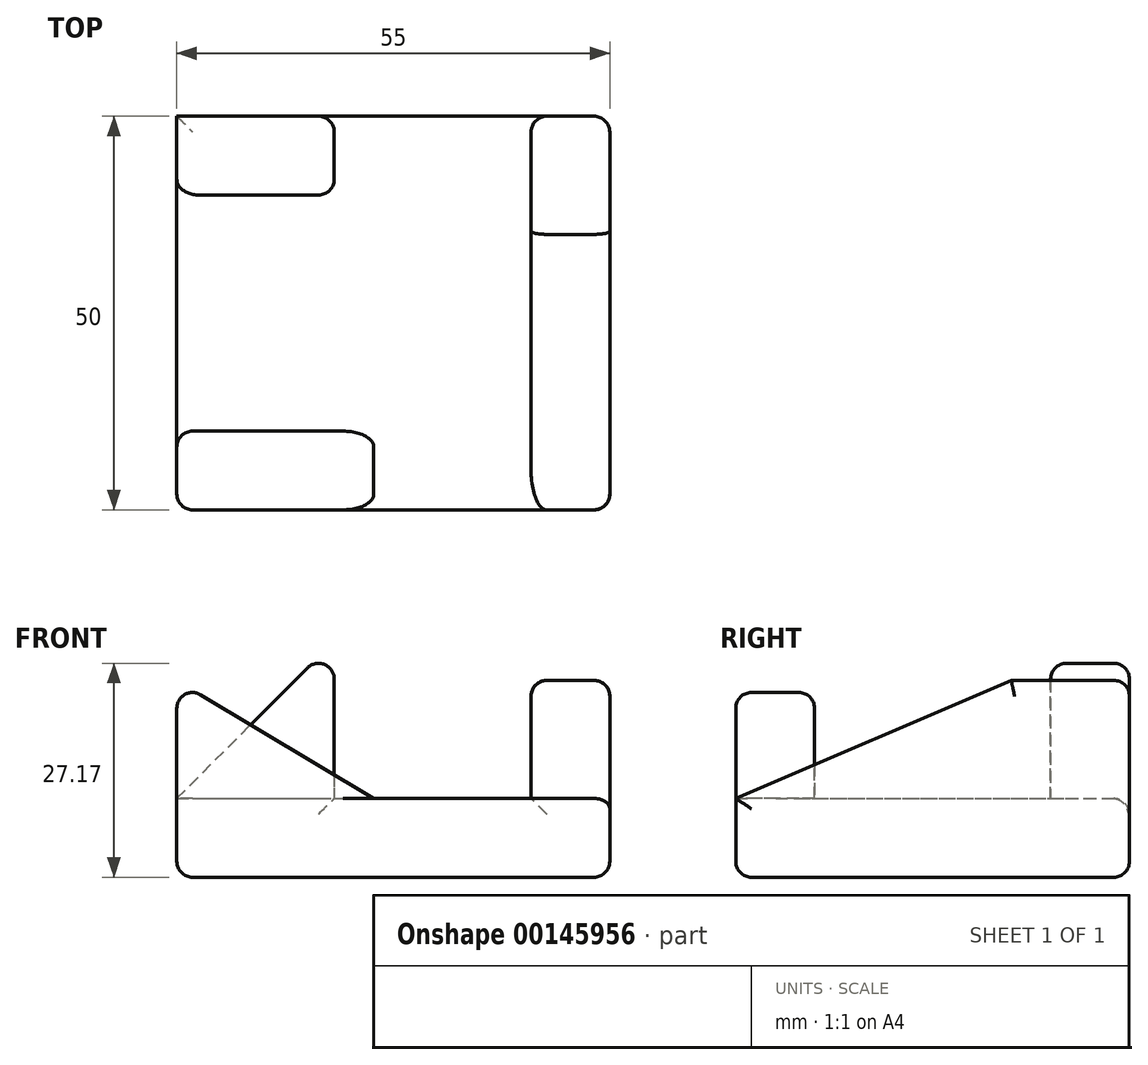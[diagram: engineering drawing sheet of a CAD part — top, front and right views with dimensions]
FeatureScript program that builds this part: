
annotation { "Feature Type Name" : "Feature", "Feature Type Description" : "" }
export const myFeature = defineFeature(function(context is Context, id is Id, definition is map)
    precondition{}
    {
        {
            var Q0;
            Q0=qCreatedBy(makeId("Top.planeOp"),FACE);
            var sketch = newSketch(context, id + "F0", { "sketchPlane" : qUnion([Q0])});
            skLineSegment(sketch, "E0.bottom", {"start": v(-27.5, -25) * mm, "end": v(27.5, -25) * mm});
            skLineSegment(sketch, "E0.top", {"start": v(-27.5, 25) * mm, "end": v(27.5, 25) * mm});
            skLineSegment(sketch, "E0.left", {"start": v(-27.5, -25) * mm, "end": v(-27.5, 25) * mm});
            skLineSegment(sketch, "E0.right", {"start": v(27.5, -25) * mm, "end": v(27.5, 25) * mm});
            skPoint(sketch, "E0.middle", {"position": v(0, 0) * mm});
            skSolve(sketch);
        }
        {
            var Q0;
            Q0 = qSketchRegion(id + "F0", true);
            extrude(context, id + "F1", {"entities" : qUnion([Q0]), "depth" : 10 * mm});
        }
        {
            var Q0;
            Q0=makeQuery(id+"F1.opExtrude","SWEPT_FACE",FACE,{"disambiguationData":[OSD([sQuery(id+"F0.wireOp",EDGE,"E0.bottom")])]});
            var sketch = newSketch(context, id + "F2", { "sketchPlane" : qUnion([Q0])});
            skLineSegment(sketch, "E1", {"start": v(-27.5, 10) * mm, "end": v(-27.5, 25) * mm});
            skLineSegment(sketch, "E2", {"start": v(-27.5, 25) * mm, "end": v(-2.5, 10) * mm});
            skLineSegment(sketch, "E3", {"start": v(-2.5, 10) * mm, "end": v(-27.5, 10) * mm});
            skSolve(sketch);
        }
        {
            var Q0;
            Q0=makeQuery(id+"F1.opExtrude","SWEPT_FACE",FACE,{"disambiguationData":[OSD([sQuery(id+"F0.wireOp",EDGE,"E0.top")])]});
            var sketch = newSketch(context, id + "F3", { "sketchPlane" : qUnion([Q0])});
            skLineSegment(sketch, "E4", {"start": v(27.5, 10) * mm, "end": v(7.5, 30) * mm});
            skLineSegment(sketch, "E5", {"start": v(7.5, 30) * mm, "end": v(7.5, 10) * mm});
            skLineSegment(sketch, "E6", {"start": v(7.5, 10) * mm, "end": v(27.5, 10) * mm});
            skSolve(sketch);
        }
        {
            var Q0;
            Q0=makeQuery(id+"F1.opExtrude","SWEPT_FACE",FACE,{"disambiguationData":[OSD([sQuery(id+"F0.wireOp",EDGE,"E0.right")])]});
            var sketch = newSketch(context, id + "F4", { "sketchPlane" : qUnion([Q0])});
            skLineSegment(sketch, "E7", {"start": v(25, 10) * mm, "end": v(25, 25) * mm});
            skLineSegment(sketch, "E8", {"start": v(25, 25) * mm, "end": v(10, 25) * mm});
            skLineSegment(sketch, "E9", {"start": v(10, 25) * mm, "end": v(-25, 10) * mm});
            skLineSegment(sketch, "E10", {"start": v(-25, 10) * mm, "end": v(25, 10) * mm});
            skSolve(sketch);
        }
        {
            var Q0;
            Q0=makeQuery(id+"F4.imprint","IMPRINT",FACE,{"disambiguationData":[TD([[makeQuery(id+"F4.imprint","IMPRINT",EDGE,{"derivedFrom":sQuery(id+"F4.wireOp",EDGE,"E7")}),1.0]])]});
            extrude(context, id + "F5", {"entities" : qUnion([Q0]), "operationType" : NewBodyOperationType.ADD, "oppositeDirection" : true, "depth" : 10 * mm});
        }
        {
            var Q0;
            Q0=makeQuery(id+"F3.imprint","IMPRINT",FACE,{"disambiguationData":[TD([[makeQuery(id+"F3.imprint","IMPRINT",EDGE,{"derivedFrom":sQuery(id+"F3.wireOp",EDGE,"E4")}),1.0]])]});
            extrude(context, id + "F6", {"entities" : qUnion([Q0]), "operationType" : NewBodyOperationType.ADD, "oppositeDirection" : true, "depth" : 10 * mm});
        }
        {
            var Q0;
            Q0=makeQuery(id+"F2.imprint","IMPRINT",FACE,{"disambiguationData":[TD([[makeQuery(id+"F2.imprint","IMPRINT",EDGE,{"derivedFrom":sQuery(id+"F2.wireOp",EDGE,"E1")}),-1.0]])]});
            extrude(context, id + "F7", {"entities" : qUnion([Q0]), "operationType" : NewBodyOperationType.ADD, "oppositeDirection" : true, "depth" : 10 * mm});
        }
        {
            var Q0;
            Q0=makeQuery(id+"F5.opExtrude","CAP_EDGE",EDGE,{"disambiguationData":[OSD([sQuery(id+"F4.wireOp",EDGE,"E7")])],"isStart":false});
            var Q1;
            Q1=makeQuery(id+"F5.opExtrude","CAP_EDGE",EDGE,{"disambiguationData":[OSD([sQuery(id+"F4.wireOp",EDGE,"E8")])],"isStart":false});
            var Q2;
            Q2=makeQuery(id+"F5.opExtrude","SWEPT_EDGE",EDGE,{"disambiguationData":[OSD([sQuery(id+"F4.wireOp",EDGE,"E7"),sQuery(id+"F4.wireOp",EDGE,"E8")])]});
            var Q3;
            Q3=makeQuery(id+"F5.boolean.opBoolean","MERGE",EDGE,{"derivedFrom":[makeQuery(id+"F1.opExtrude","SWEPT_EDGE",EDGE,{"disambiguationData":[OSD([sQuery(id+"F0.wireOp",EDGE,"E0.top"),sQuery(id+"F0.wireOp",EDGE,"E0.right")])]}),makeQuery(id+"F5.opExtrude","CAP_EDGE",EDGE,{"disambiguationData":[OSD([sQuery(id+"F4.wireOp",EDGE,"E7")])],"isStart":true})]});
            var Q4;
            Q4=makeQuery(id+"F5.opExtrude","CAP_EDGE",EDGE,{"disambiguationData":[OSD([sQuery(id+"F4.wireOp",EDGE,"E8")])],"isStart":true});
            var Q5;
            Q5=makeQuery(id+"F5.opExtrude","CAP_EDGE",EDGE,{"disambiguationData":[OSD([sQuery(id+"F4.wireOp",EDGE,"E9")])],"isStart":false});
            var Q6;
            Q6=makeQuery(id+"F5.opExtrude","CAP_EDGE",EDGE,{"disambiguationData":[OSD([sQuery(id+"F4.wireOp",EDGE,"E9")])],"isStart":true});
            var Q7;
            Q7=makeQuery(id+"F6.opExtrude","CAP_EDGE",EDGE,{"disambiguationData":[OSD([sQuery(id+"F3.wireOp",EDGE,"E4")])],"isStart":true});
            var Q8;
            Q8=makeQuery(id+"F6.opExtrude","CAP_EDGE",EDGE,{"disambiguationData":[OSD([sQuery(id+"F3.wireOp",EDGE,"E4")])],"isStart":false});
            var Q9;
            Q9=makeQuery(id+"F6.opExtrude","SWEPT_EDGE",EDGE,{"disambiguationData":[OSD([sQuery(id+"F3.wireOp",EDGE,"E4"),sQuery(id+"F3.wireOp",EDGE,"E5")])]});
            var Q10;
            Q10=makeQuery(id+"F6.opExtrude","CAP_EDGE",EDGE,{"disambiguationData":[OSD([sQuery(id+"F3.wireOp",EDGE,"E5")])],"isStart":true});
            var Q11;
            Q11=makeQuery(id+"F1.opExtrude","CAP_EDGE",EDGE,{"disambiguationData":[OSD([sQuery(id+"F0.wireOp",EDGE,"E0.top")])],"isStart":false});
            var Q12;
            Q12=makeQuery(id+"F6.opExtrude","CAP_EDGE",EDGE,{"disambiguationData":[OSD([sQuery(id+"F3.wireOp",EDGE,"E5")])],"isStart":false});
            var Q13;
            Q13=makeQuery(id+"F1.opExtrude","CAP_EDGE",EDGE,{"disambiguationData":[OSD([sQuery(id+"F0.wireOp",EDGE,"E0.left")])],"isStart":true});
            var Q14;
            Q14=makeQuery(id+"F7.opExtrude","CAP_EDGE",EDGE,{"disambiguationData":[OSD([sQuery(id+"F2.wireOp",EDGE,"E1")])],"isStart":false});
            var Q15;
            Q15=makeQuery(id+"F7.opExtrude","CAP_EDGE",EDGE,{"disambiguationData":[OSD([sQuery(id+"F2.wireOp",EDGE,"E2")])],"isStart":false});
            var Q16;
            Q16=makeQuery(id+"F7.opExtrude","SWEPT_EDGE",EDGE,{"disambiguationData":[OSD([sQuery(id+"F2.wireOp",EDGE,"E1"),sQuery(id+"F2.wireOp",EDGE,"E2")])]});
            var Q17;
            Q17=makeQuery(id+"F7.boolean.opBoolean","MERGE",EDGE,{"derivedFrom":[makeQuery(id+"F1.opExtrude","SWEPT_EDGE",EDGE,{"disambiguationData":[OSD([sQuery(id+"F0.wireOp",EDGE,"E0.bottom"),sQuery(id+"F0.wireOp",EDGE,"E0.left")])]}),makeQuery(id+"F7.opExtrude","CAP_EDGE",EDGE,{"disambiguationData":[OSD([sQuery(id+"F2.wireOp",EDGE,"E1")])],"isStart":true})]});
            var Q18;
            Q18=makeQuery(id+"F7.opExtrude","CAP_EDGE",EDGE,{"disambiguationData":[OSD([sQuery(id+"F2.wireOp",EDGE,"E2")])],"isStart":true});
            var Q19;
            Q19=makeQuery(id+"F1.opExtrude","CAP_EDGE",EDGE,{"disambiguationData":[OSD([sQuery(id+"F0.wireOp",EDGE,"E0.bottom")])],"isStart":true});
            var Q20;
            Q20=makeQuery(id+"F1.opExtrude","SWEPT_EDGE",EDGE,{"disambiguationData":[OSD([sQuery(id+"F0.wireOp",EDGE,"E0.bottom"),sQuery(id+"F0.wireOp",EDGE,"E0.right")])]});
            var Q21;
            Q21=makeQuery(id+"F1.opExtrude","CAP_EDGE",EDGE,{"disambiguationData":[OSD([sQuery(id+"F0.wireOp",EDGE,"E0.right")])],"isStart":true});
            var Q22;
            Q22=makeQuery(id+"F1.opExtrude","CAP_EDGE",EDGE,{"disambiguationData":[OSD([sQuery(id+"F0.wireOp",EDGE,"E0.top")])],"isStart":true});
            fillet(context, id + "F8", {"entities" : qUnion([Q0, Q1, Q2, Q3, Q4, Q5, Q6, Q7, Q8, Q9, Q10, Q11, Q12, Q13, Q14, Q15, Q16, Q17, Q18, Q19, Q20, Q21, Q22]), "radius" : 2 * mm, "tangentPropagation" : true, "allowEdgeOverflow" : false});
        }
    });
